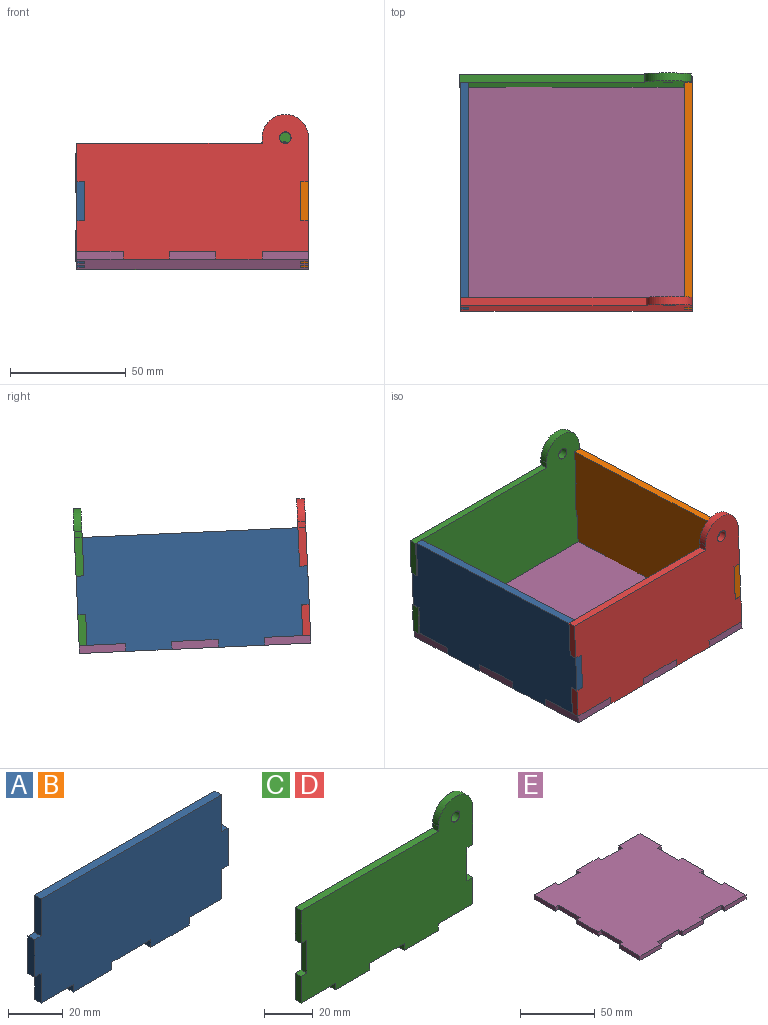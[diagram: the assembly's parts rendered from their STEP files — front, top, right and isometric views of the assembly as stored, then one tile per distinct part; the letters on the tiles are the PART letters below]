
ASSEMBLY  parts=5 mates=4
PART A: 22 faces, bbox 100x3.4x50 mm
  f0: plane 3.4x3.4mm, normal (-1,0,0), area 11.6mm2, adj f1,f19,f20,f21
  f1: plane 20x3.4mm, normal (0,0,-1), area 68mm2, adj f0,f2,f20,f21
  f2: plane 3.4x3.4mm, normal (1,0,0), area 11.6mm2, adj f1,f3,f20,f21
  f3: plane 16.6x3.4mm, normal (0,0,-1), area 56.4mm2, adj f2,f4,f20,f21
  f4: plane 13.2x3.4mm, normal (1,0,0), area 44.9mm2, adj f3,f5,f20,f21
  f5: plane 3.4x3.4mm, normal (0,0,-1), area 11.6mm2, adj f4,f6,f20,f21
  f6: plane 16.8x3.4mm, normal (1,0,0), area 57.1mm2, adj f5,f7,f20,f21
  f7: plane 3.4x3.4mm, normal (0,0,1), area 11.6mm2, adj f6,f8,f20,f21
  f8: plane 16.6x3.4mm, normal (1,0,0), area 56.4mm2, adj f7,f9,f20,f21
  f9: plane 93.2x3.4mm, normal (0,0,1), area 316.9mm2, adj f8,f10,f20,f21
  f10: plane 16.6x3.4mm, normal (-1,0,0), area 56.4mm2, adj f9,f11,f20,f21
  f11: plane 3.4x3.4mm, normal (0,0,1), area 11.6mm2, adj f10,f12,f20,f21
  f12: plane 16.8x3.4mm, normal (-1,0,0), area 57.1mm2, adj f11,f13,f20,f21
  f13: plane 3.4x3.4mm, normal (0,0,-1), area 11.6mm2, adj f12,f14,f20,f21
  f14: plane 13.2x3.4mm, normal (-1,0,0), area 44.9mm2, adj f13,f15,f20,f21
  f15: plane 16.6x3.4mm, normal (0,0,-1), area 56.4mm2, adj f14,f16,f20,f21
  f16: plane 3.4x3.4mm, normal (-1,0,0), area 11.6mm2, adj f15,f17,f20,f21
  f17: plane 20x3.4mm, normal (0,0,-1), area 68mm2, adj f16,f18,f20,f21
  f18: plane 3.4x3.4mm, normal (1,0,0), area 11.6mm2, adj f17,f19,f20,f21
  f19: plane 20x3.4mm, normal (0,0,-1), area 68mm2, adj f0,f18,f20,f21
  f20: plane 100x50mm, normal (0,-1,0), area 4593.4mm2, adj f0,f1,f2,f3,f4,f5,f6,f7
  f21: plane 100x50mm, normal (0,1,0), area 4593.4mm2, adj f0,f1,f2,f3,f4,f5,f6,f7
PART B: same geometry as A
PART C: 25 faces, bbox 100x3.4x62.5 mm
  f0: plane 16.6x3.4mm, normal (-1,0,0), area 56.4mm2, adj f1,f19,f20,f21
  f1: plane 3.4x3.4mm, normal (0,0,-1), area 11.6mm2, adj f0,f2,f20,f21
  f2: plane 16.6x3.4mm, normal (-1,0,0), area 56.4mm2, adj f1,f3,f20,f21
  f3: plane 3.4x3.4mm, normal (0,0,1), area 11.6mm2, adj f2,f4,f20,f21
  f4: plane 13.4x3.4mm, normal (-1,0,0), area 45.6mm2, adj f3,f5,f20,f21
  f5: plane 20x3.4mm, normal (0,0,-1), area 68mm2, adj f4,f6,f20,f21
  f6: plane 3.4x3.4mm, normal (-1,0,0), area 11.6mm2, adj f5,f7,f20,f21
  f7: plane 20x3.4mm, normal (0,0,-1), area 68mm2, adj f6,f8,f20,f21
  f8: plane 3.4x3.4mm, normal (1,0,0), area 11.6mm2, adj f7,f9,f20,f21
  f9: plane 20x3.4mm, normal (0,0,-1), area 68mm2, adj f8,f10,f20,f21
  f10: plane 3.4x3.4mm, normal (-1,0,0), area 11.6mm2, adj f9,f11,f20,f21
  f11: plane 20x3.4mm, normal (0,0,-1), area 68mm2, adj f10,f12,f20,f21
  f12: plane 3.4x3.4mm, normal (1,0,0), area 11.6mm2, adj f11,f13,f20,f21
  f13: plane 20x3.4mm, normal (0,0,-1), area 68mm2, adj f12,f14,f20,f21
  f14: plane 13.4x3.4mm, normal (1,0,0), area 45.6mm2, adj f13,f15,f20,f21
  f15: plane 3.4x3.4mm, normal (0,0,1), area 11.6mm2, adj f14,f16,f20,f21
  f16: plane 16.6x3.4mm, normal (1,0,0), area 56.4mm2, adj f15,f17,f20,f21
  f17: plane 3.4x3.4mm, normal (0,0,-1), area 11.6mm2, adj f16,f18,f20,f21
  f18: plane 19.1x3.4mm, normal (1,0,0), area 64.9mm2, adj f17,f20,f21,f23
  f19: plane 80x3.4mm, normal (0,0,1), area 272mm2, adj f0,f20,f21,f22
  f20: plane 100x62.5mm, normal (0,-1,0), area 4870.6mm2, adj f0,f1,f2,f3,f4,f5,f6,f7
  f21: plane 100x62.5mm, normal (0,1,0), area 4870.6mm2, adj f0,f1,f2,f3,f4,f5,f6,f7
  f22: plane 3.4x2.5mm, normal (-1,0,0), area 8.5mm2, adj f19,f20,f21,f23
  f23: cylinder r=10mm len=20mm, axis (0,-1,0), area 106.8mm2, adj f18,f20,f21,f22
  f24: cylinder r=2.5mm len=5mm, axis (0,-1,0), area 53.4mm2, adj f20,f21
PART D: same geometry as C
PART E: 38 faces, bbox 100x100x3.4 mm
  f0: plane 3.4x3.4mm, normal (1,0,0), area 11.6mm2, adj f1,f35,f36,f37
  f1: plane 20x3.4mm, normal (0,1,0), area 68mm2, adj f0,f2,f36,f37
  f2: plane 20x3.4mm, normal (-1,0,0), area 68mm2, adj f1,f3,f36,f37
  f3: plane 3.4x3.4mm, normal (0,-1,0), area 11.6mm2, adj f2,f4,f36,f37
  f4: plane 20x3.4mm, normal (-1,0,0), area 68mm2, adj f3,f5,f36,f37
  f5: plane 3.4x3.4mm, normal (0,1,0), area 11.6mm2, adj f4,f6,f36,f37
  f6: plane 20.51x3.4mm, normal (-1,0,0), area 69.7mm2, adj f5,f7,f36,f37
  f7: plane 3.4x3.4mm, normal (0,-1,0), area 11.6mm2, adj f6,f8,f36,f37
  f8: plane 20x3.4mm, normal (-1,0,0), area 68mm2, adj f7,f9,f36,f37
  f9: plane 3.4x3.4mm, normal (0,1,0), area 11.6mm2, adj f8,f10,f36,f37
  f10: plane 19.49x3.4mm, normal (-1,0,0), area 66.3mm2, adj f9,f11,f36,f37
  f11: plane 20x3.4mm, normal (0,-1,0), area 68mm2, adj f10,f12,f36,f37
  f12: plane 3.4x3.4mm, normal (1,0,0), area 11.6mm2, adj f11,f13,f36,f37
  f13: plane 20x3.4mm, normal (0,-1,0), area 68mm2, adj f12,f14,f36,f37
  f14: plane 3.4x3.4mm, normal (-1,0,0), area 11.6mm2, adj f13,f15,f36,f37
  f15: plane 20x3.4mm, normal (0,-1,0), area 68mm2, adj f14,f16,f36,f37
  f16: plane 3.4x3.4mm, normal (1,0,0), area 11.6mm2, adj f15,f17,f36,f37
  f17: plane 20x3.4mm, normal (0,-1,0), area 68mm2, adj f16,f18,f36,f37
  f18: plane 3.4x3.4mm, normal (-1,0,0), area 11.6mm2, adj f17,f19,f36,f37
  f19: plane 20x3.4mm, normal (0,-1,0), area 68mm2, adj f18,f20,f36,f37
  f20: plane 20x3.4mm, normal (1,0,0), area 68mm2, adj f19,f21,f36,f37
  f21: plane 3.4x3.4mm, normal (0,1,0), area 11.6mm2, adj f20,f22,f36,f37
  f22: plane 20x3.4mm, normal (1,0,0), area 68mm2, adj f21,f23,f36,f37
  f23: plane 3.4x3.4mm, normal (0,-1,0), area 11.6mm2, adj f22,f24,f36,f37
  f24: plane 20x3.4mm, normal (1,0,0), area 68mm2, adj f23,f25,f36,f37
  f25: plane 3.4x3.4mm, normal (0,1,0), area 11.6mm2, adj f24,f26,f36,f37
  f26: plane 20x3.4mm, normal (1,0,0), area 68mm2, adj f25,f27,f36,f37
  f27: plane 3.4x3.4mm, normal (0,-1,0), area 11.6mm2, adj f26,f28,f36,f37
  f28: plane 20x3.4mm, normal (1,0,0), area 68mm2, adj f27,f29,f36,f37
  f29: plane 20x3.4mm, normal (0,1,0), area 68mm2, adj f28,f30,f36,f37
  f30: plane 3.4x3.4mm, normal (-1,0,0), area 11.6mm2, adj f29,f31,f36,f37
  f31: plane 19.46x3.4mm, normal (0,1,0), area 66.2mm2, adj f30,f32,f36,f37
  f32: plane 3.4x3.4mm, normal (1,0,0), area 11.6mm2, adj f31,f33,f36,f37
  f33: plane 20.54x3.4mm, normal (0,1,0), area 69.8mm2, adj f32,f34,f36,f37
  f34: plane 3.4x3.4mm, normal (-1,0,0), area 11.6mm2, adj f33,f35,f36,f37
  f35: plane 20x3.4mm, normal (0,1,0), area 68mm2, adj f0,f34,f36,f37
  f36: plane 100x100mm, normal (0,0,1), area 9457.8mm2, adj f0,f1,f2,f3,f4,f5,f6,f7
  f37: plane 100x100mm, normal (0,0,-1), area 9457.8mm2, adj f0,f1,f2,f3,f4,f5,f6,f7
PLACE A rot(axis=(-0.02,-0.02,-1),90deg) t=(9.69,22.03,39.27)mm
PLACE B rot(axis=(-0.02,-0.02,-1),90deg) t=(106.29,22.03,39.27)mm
PLACE C rot(axis=(-1,0,0),2.6deg) t=(61.44,61.25,20.92)mm
PLACE D rot(axis=(-1,0,0),2.6deg) t=(61.96,-35.26,25.25)mm
PLACE E rot(axis=(-0.02,-0.02,-1),90deg) t=(6.29,60.27,-0.87)mm
MATE fastened C.f20 <-> E.f8  axis (0,1,-0.04) through (25.78,56.87,-0.71)mm
MATE fastened A.f18 <-> E.f14  axis (0,-1,0.04) through (7.99,20.39,2.63)mm
MATE fastened B.f16 <-> E.f0  axis (0,1,-0.04) through (104.59,40.37,1.73)mm
MATE fastened D.f10 <-> E.f25  axis (-1,0,0) through (66.29,-37.86,5.24)mm
